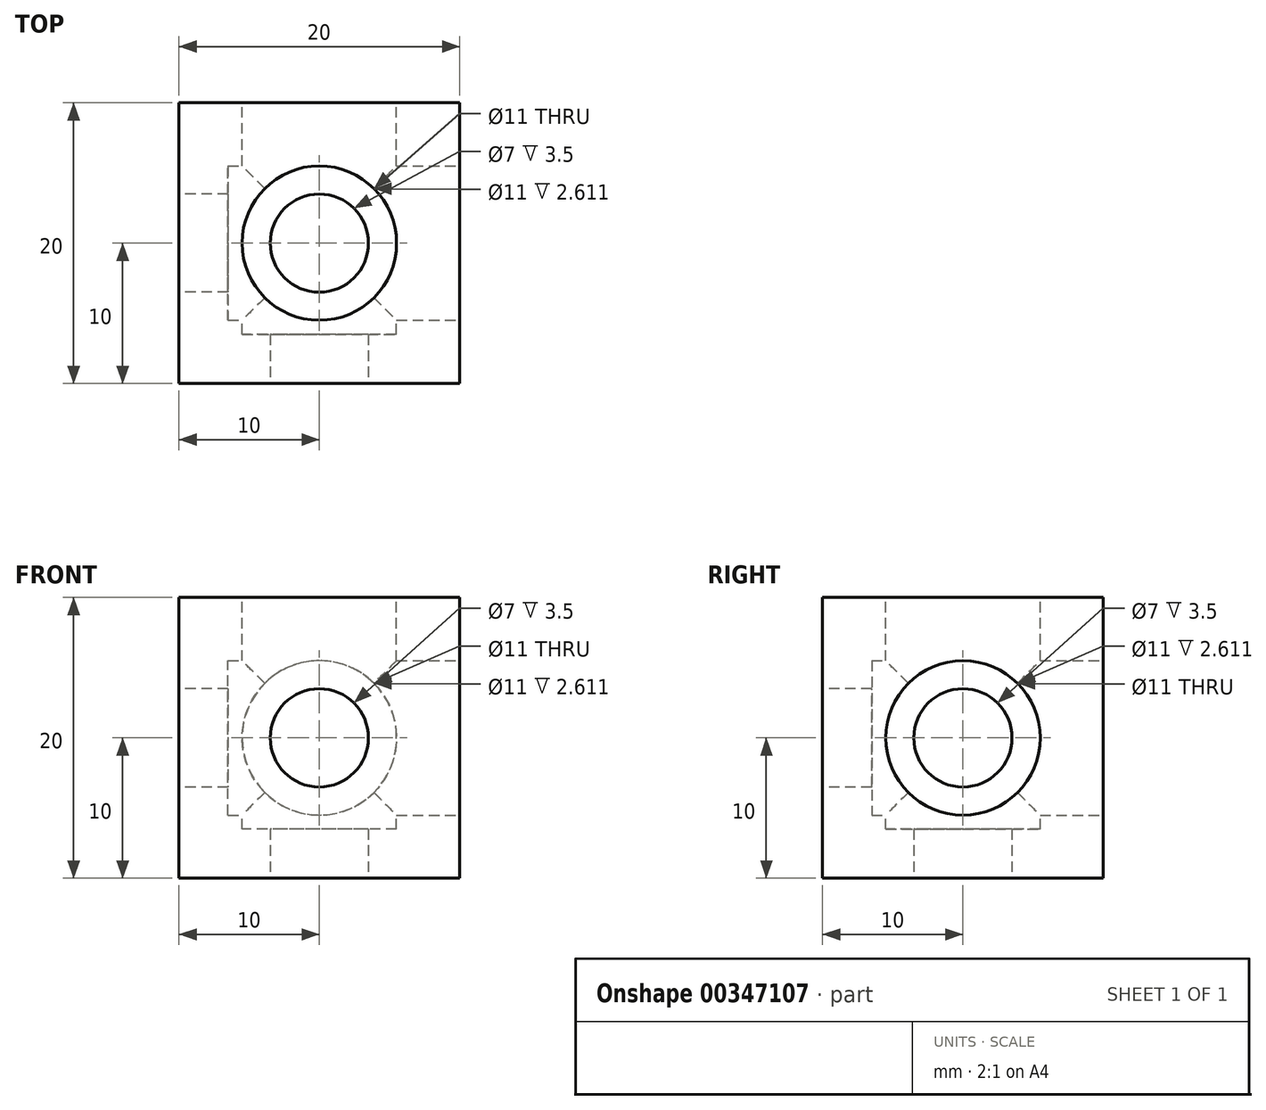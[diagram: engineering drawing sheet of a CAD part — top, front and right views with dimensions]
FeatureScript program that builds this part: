
annotation { "Feature Type Name" : "Feature", "Feature Type Description" : "" }
export const myFeature = defineFeature(function(context is Context, id is Id, definition is map)
    precondition{}
    {
        {
            var Q0;
            Q0=qCreatedBy(makeId("Top.planeOp"),FACE);
            var sketch = newSketch(context, id + "F0", { "sketchPlane" : qUnion([Q0])});
            skLineSegment(sketch, "E0.bottom", {"start": v(-10, 10) * mm, "end": v(10, 10) * mm});
            skLineSegment(sketch, "E0.top", {"start": v(-10, -10) * mm, "end": v(10, -10) * mm});
            skLineSegment(sketch, "E0.left", {"start": v(-10, 10) * mm, "end": v(-10, -10) * mm});
            skLineSegment(sketch, "E0.right", {"start": v(10, 10) * mm, "end": v(10, -10) * mm});
            skPoint(sketch, "E0.middle", {"position": v(0, 0) * mm});
            skCircle(sketch, "E1", {"center": v(0, 0) * mm, "radius": 3.5 * mm});
            skSolve(sketch);
        }
        {
            var Q0;
            Q0=makeQuery(id+"F0.imprint","IMPRINT",FACE,{"disambiguationData":[TD([[makeQuery(id+"F0.imprint","IMPRINT",EDGE,{"derivedFrom":sQuery(id+"F0.wireOp",EDGE,"E0.bottom")}),-1.0]])]});
            extrude(context, id + "F1", {"entities" : qUnion([Q0]), "depth" : 20 * mm});
        }
        {
            var Q0;
            Q0=makeQuery(id+"F1.opExtrude","SWEPT_FACE",FACE,{"disambiguationData":[OSD([sQuery(id+"F0.wireOp",EDGE,"E0.top")])]});
            var sketch = newSketch(context, id + "F2", { "sketchPlane" : qUnion([Q0])});
            skCircle(sketch, "E2", {"center": v(0, 10) * mm, "radius": 3.5 * mm});
            skPoint(sketch, "E2.centerSnap0", {"position": v(-10, 10) * mm});
            skPoint(sketch, "E2.centerSnap1", {"position": v(0, 0) * mm});
            skSolve(sketch);
        }
        {
            var Q0;
            Q0=makeQuery(id+"F2.imprint","IMPRINT",FACE,{"disambiguationData":[TD([[makeQuery(id+"F2.imprint","IMPRINT",EDGE,{"derivedFrom":sQuery(id+"F2.wireOp",EDGE,"E2")}),1.0]])]});
            extrude(context, id + "F3", {"entities" : qUnion([Q0]), "operationType" : NewBodyOperationType.REMOVE, "oppositeDirection" : true, "depth" : 20 * mm});
        }
        {
            var Q0;
            Q0=makeQuery(id+"F1.opExtrude","SWEPT_FACE",FACE,{"disambiguationData":[OSD([sQuery(id+"F0.wireOp",EDGE,"E0.left")])]});
            var sketch = newSketch(context, id + "F4", { "sketchPlane" : qUnion([Q0])});
            skCircle(sketch, "E3", {"center": v(0, 10) * mm, "radius": 3.5 * mm});
            skPoint(sketch, "E3.centerSnap0", {"position": v(10, 10) * mm});
            skSolve(sketch);
        }
        {
            var Q0;
            Q0=makeQuery(id+"F4.imprint","IMPRINT",FACE,{"disambiguationData":[TD([[makeQuery(id+"F4.imprint","IMPRINT",EDGE,{"derivedFrom":sQuery(id+"F4.wireOp",EDGE,"E3")}),1.0]])]});
            extrude(context, id + "F5", {"entities" : qUnion([Q0]), "operationType" : NewBodyOperationType.REMOVE, "oppositeDirection" : true, "depth" : 20 * mm});
        }
        {
            var Q0;
            Q0=makeQuery(id+"F1.opExtrude","CAP_FACE",FACE,{"disambiguationData":[OSD([sQuery(id+"F0.wireOp",EDGE,"E0.bottom"),sQuery(id+"F0.wireOp",EDGE,"E0.top"),sQuery(id+"F0.wireOp",EDGE,"E0.left"),sQuery(id+"F0.wireOp",EDGE,"E0.right"),sQuery(id+"F0.wireOp",EDGE,"E1")])],"isStart":false});
            var sketch = newSketch(context, id + "F6", { "sketchPlane" : qUnion([Q0])});
            skCircle(sketch, "E4", {"center": v(0, 0) * mm, "radius": 5.5 * mm});
            skSolve(sketch);
        }
        {
            var Q0;
            Q0=makeQuery(id+"F6.imprint","IMPRINT",FACE,{"disambiguationData":[TD([[makeQuery(id+"F6.imprint","IMPRINT",EDGE,{"derivedFrom":sQuery(id+"F6.wireOp",EDGE,"E4")}),1.0]])]});
            extrude(context, id + "F7", {"entities" : qUnion([Q0]), "operationType" : NewBodyOperationType.REMOVE, "oppositeDirection" : true, "depth" : 16.5 * mm});
        }
        {
            var Q0;
            Q0=makeQuery(id+"F1.opExtrude","SWEPT_FACE",FACE,{"disambiguationData":[OSD([sQuery(id+"F0.wireOp",EDGE,"E0.bottom")])]});
            var sketch = newSketch(context, id + "F8", { "sketchPlane" : qUnion([Q0])});
            skCircle(sketch, "E5", {"center": v(0, 10) * mm, "radius": 5.5 * mm});
            skSolve(sketch);
        }
        {
            var Q0;
            Q0=makeQuery(id+"F8.imprint","IMPRINT",FACE,{"disambiguationData":[TD([[makeQuery(id+"F8.imprint","IMPRINT",EDGE,{"derivedFrom":sQuery(id+"F8.wireOp",EDGE,"E5")}),1.0]])]});
            extrude(context, id + "F9", {"entities" : qUnion([Q0]), "operationType" : NewBodyOperationType.REMOVE, "oppositeDirection" : true, "depth" : 16.5 * mm});
        }
        {
            var Q0;
            Q0=makeQuery(id+"F1.opExtrude","SWEPT_FACE",FACE,{"disambiguationData":[OSD([sQuery(id+"F0.wireOp",EDGE,"E0.right")])]});
            var sketch = newSketch(context, id + "F10", { "sketchPlane" : qUnion([Q0])});
            skCircle(sketch, "E6", {"center": v(0, 10) * mm, "radius": 5.5 * mm});
            skSolve(sketch);
        }
        {
            var Q0;
            Q0=makeQuery(id+"F10.imprint","IMPRINT",FACE,{"disambiguationData":[TD([[makeQuery(id+"F10.imprint","IMPRINT",EDGE,{"derivedFrom":sQuery(id+"F10.wireOp",EDGE,"E6")}),1.0]])]});
            extrude(context, id + "F11", {"entities" : qUnion([Q0]), "operationType" : NewBodyOperationType.REMOVE, "oppositeDirection" : true, "depth" : 16.5 * mm});
        }
    });
